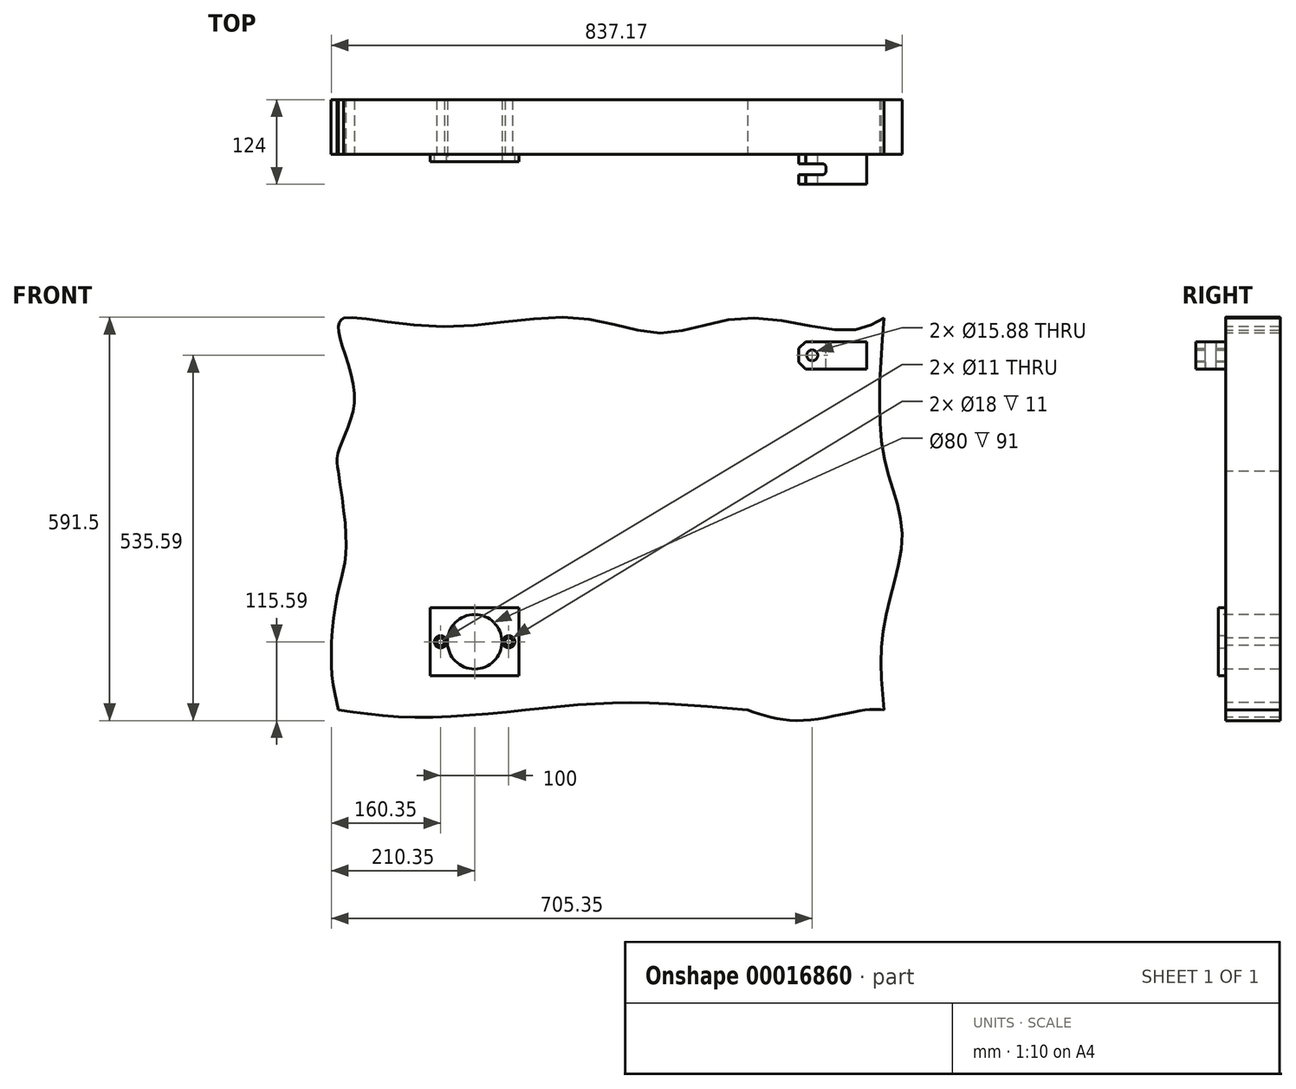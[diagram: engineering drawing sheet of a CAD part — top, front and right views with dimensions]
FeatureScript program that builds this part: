
annotation { "Feature Type Name" : "Feature", "Feature Type Description" : "" }
export const myFeature = defineFeature(function(context is Context, id is Id, definition is map)
    precondition{}
    {
        {
            var Q0;
            Q0=qCreatedBy(makeId("Front.planeOp"),FACE);
            var sketch = newSketch(context, id + "F0", { "sketchPlane" : qUnion([Q0])});
            skPoint(sketch, "E0.rect.middle", {"position": v(0, 0) * mm});
            skFitSpline(sketch, "E1", {"points": [v(-300, 175) * mm, v(-288.67, 56.04) * mm, v(-300, 0) * mm, v(-310.2, -107.97) * mm, v(-300, -175) * mm], "startDerivative": vector(67.45, -453.57) * mm, "endDerivative": vector(63.04, -272.45) * mm});
            skFitSpline(sketch, "E2", {"points": [v(300, -175) * mm, v(120.43, -164.33) * mm, v(-25.86, -175) * mm, v(-186.7, -185.87) * mm, v(-300, -175) * mm], "startDerivative": vector(-676.6, 60.09) * mm, "endDerivative": vector(-491.54, 71) * mm});
            skLineSegment(sketch, "E3", {"start": v(0, 0) * mm, "end": v(0, -225.11) * mm, "construction": true});
            skLineSegment(sketch, "E4", {"start": v(0, 0) * mm, "end": v(412.09, 0) * mm, "construction": true});
            skLineSegment(sketch, "E5.0", {"start": v(0, 400) * mm, "end": v(412.09, 400) * mm, "construction": true});
            skLineSegment(sketch, "E6.0", {"start": v(500, 0) * mm, "end": v(500, -225.11) * mm, "construction": true});
            skFitSpline(sketch, "E7", {"points": [v(-300, 175) * mm, v(-300, 203.47) * mm, v(-276.37, 283.03) * mm, v(-300, 385.32) * mm, v(-292.47, 400) * mm], "startDerivative": vector(-24.62, 139.08) * mm, "endDerivative": vector(79.67, 74.73) * mm});
            skFitSpline(sketch, "E8", {"points": [v(300, -175) * mm, v(377.16, -190.54) * mm, v(471.87, -175) * mm, v(500, -175) * mm], "startDerivative": vector(193.63, -65.98) * mm, "endDerivative": vector(105.88, -11.33) * mm});
            skFitSpline(sketch, "E9", {"points": [v(-292.47, 400) * mm, v(-271.63, 400) * mm, v(-139.98, 387.21) * mm, v(50.4, 400) * mm, v(177.31, 377.74) * mm, v(297.6, 400) * mm, v(448.2, 381.53) * mm, v(500, 400) * mm], "startDerivative": vector(259.87, 21.6) * mm, "endDerivative": vector(420.11, 258.52) * mm});
            skFitSpline(sketch, "E10", {"points": [v(500, 400) * mm, v(500, 197.79) * mm, v(526.8, 82.23) * mm, v(500, -51.31) * mm, v(500, -175) * mm], "startDerivative": vector(-55.22, -736.49) * mm, "endDerivative": vector(47.01, -523.19) * mm});
            skSolve(sketch);
        }
        {
            var Q0;
            Q0=qSketchRegion(id+"F0",true);
            extrude(context, id + "F1", {"entities" : qUnion([Q0]), "oppositeDirection" : true, "depth" : 80 * mm});
        }
        {
            var Q0;
            Q0=makeQuery(id+"F1.opExtrude","CAP_FACE",FACE,{"disambiguationData":[OSD([sQuery(id+"F0.wireOp",EDGE,"E1"),sQuery(id+"F0.wireOp",EDGE,"bc24038a-8613-4d95-baf4-b4a1aed5c15a"),sQuery(id+"F0.wireOp",EDGE,"fdfd1424-a203-45f8-9f44-afd27f2000e9"),sQuery(id+"F0.wireOp",EDGE,"E2")])],"isStart":true});
            var sketch = newSketch(context, id + "F2", { "sketchPlane" : qUnion([Q0])});
            skLineSegment(sketch, "E11", {"start": v(-100, 270) * mm, "end": v(-100, -299.44) * mm, "construction": true});
            skLineSegment(sketch, "E12", {"start": v(-457.85, -75) * mm, "end": v(206.33, -75) * mm, "construction": true});
            skCircle(sketch, "E13", {"center": v(-100, -75) * mm, "radius": 40 * mm});
            skLineSegment(sketch, "E14.0", {"start": v(-150, 270) * mm, "end": v(-150, -299.44) * mm, "construction": true});
            skCircle(sketch, "E15", {"center": v(-150, -75) * mm, "radius": 5.5 * mm});
            skCircle(sketch, "E16.0.MirrorC", {"center": v(-50, -75) * mm, "radius": 5.5 * mm});
            skSolve(sketch);
        }
        {
            var Q0;
            Q0=qSketchRegion(id+"F2",true);
            extrude(context, id + "F3", {"entities" : qUnion([Q0]), "operationType" : NewBodyOperationType.REMOVE, "endBound" : BoundingType.THROUGH_ALL, "oppositeDirection" : true, "depth" : 25 * mm});
        }
        {
            var Q0;
            Q0=makeQuery(id+"F1.opExtrude","CAP_FACE",FACE,{"disambiguationData":[OSD([sQuery(id+"F0.wireOp",EDGE,"E1"),sQuery(id+"F0.wireOp",EDGE,"bc24038a-8613-4d95-baf4-b4a1aed5c15a"),sQuery(id+"F0.wireOp",EDGE,"fdfd1424-a203-45f8-9f44-afd27f2000e9"),sQuery(id+"F0.wireOp",EDGE,"E2")])],"isStart":true});
            var sketch = newSketch(context, id + "F4", { "sketchPlane" : qUnion([Q0])});
            skLineSegment(sketch, "E17", {"start": v(-100, -75) * mm, "end": v(-100, -205.65) * mm, "construction": true});
            skLineSegment(sketch, "E18", {"start": v(-100, -75) * mm, "end": v(-353.74, -75) * mm, "construction": true});
            skLineSegment(sketch, "E19.0", {"start": v(-165, -25) * mm, "end": v(-165, -125) * mm});
            skLineSegment(sketch, "E20.0", {"start": v(-35, -125) * mm, "end": v(-165, -125) * mm});
            skLineSegment(sketch, "E21.0.MirrorCS", {"start": v(-35, -25) * mm, "end": v(-165, -25) * mm});
            skLineSegment(sketch, "E22.0.MirrorCS", {"start": v(-35, -25) * mm, "end": v(-35, -125) * mm});
            skPoint(sketch, "E23.orphan", {"position": v(-165, -75) * mm});
            skPoint(sketch, "E24.orphan", {"position": v(-100, -25) * mm});
            skPoint(sketch, "E25.orphan", {"position": v(-35, -75) * mm});
            skPoint(sketch, "E26.orphan", {"position": v(-100, -125) * mm});
            skPoint(sketch, "E27.orphan", {"position": v(-353.74, -25) * mm});
            skPoint(sketch, "E28.orphan", {"position": v(-353.74, -125) * mm});
            skPoint(sketch, "E29.orphan", {"position": v(-165, -205.65) * mm});
            skPoint(sketch, "E30.orphan", {"position": v(-35, -205.65) * mm});
            skCircle(sketch, "E31.0", {"center": v(-100, -75) * mm, "radius": 40 * mm});
            skCircle(sketch, "E32", {"center": v(-150, -75) * mm, "radius": 9 * mm});
            skCircle(sketch, "E33.0.MirrorC", {"center": v(-50, -75) * mm, "radius": 9 * mm});
            skSolve(sketch);
        }
        {
            var Q0;
            Q0=qSketchRegion(id+"F4",true);
            extrude(context, id + "F5", {"entities" : qUnion([Q0]), "operationType" : NewBodyOperationType.ADD, "depth" : 11 * mm});
        }
        {
            var Q0;
            {var subQ0=sQuery(id+"F0.wireOp",EDGE,"E1");var subQ1=sQuery(id+"F0.wireOp",EDGE,"bc24038a-8613-4d95-baf4-b4a1aed5c15a");var subQ2=sQuery(id+"F0.wireOp",EDGE,"fdfd1424-a203-45f8-9f44-afd27f2000e9");var subQ3=sQuery(id+"F0.wireOp",EDGE,"E2");Q0=makeQuery(id+"F5.boolean.opBoolean","SPLIT",FACE,{"disambiguationData":[TD([makeQuery(id+"F1.opExtrude","SWEPT_FACE",FACE,{"disambiguationData":[OSD([subQ0])]})])],"derivedFrom":makeQuery(id+"F1.opExtrude","CAP_FACE",FACE,{"disambiguationData":[OSD([subQ0,subQ1,subQ2,subQ3])],"isStart":true})});}
            var sketch = newSketch(context, id + "F6", { "sketchPlane" : qUnion([Q0])});
            skCircle(sketch, "E34.0", {"center": v(-100, -75) * mm, "radius": 40 * mm, "construction": true});
            skLineSegment(sketch, "E35", {"start": v(-100, -75) * mm, "end": v(-100, 236.24) * mm, "construction": true});
            skLineSegment(sketch, "E36", {"start": v(-100, -75) * mm, "end": v(374.63, -75) * mm, "construction": true});
            skLineSegment(sketch, "E37.0", {"start": v(375, -75) * mm, "end": v(375, 236.24) * mm, "construction": true});
            skLineSegment(sketch, "E38.0", {"start": v(-100, 325) * mm, "end": v(374.63, 325) * mm, "construction": true});
            skLineSegment(sketch, "E39.0", {"start": v(475, -75) * mm, "end": v(475, 236.24) * mm, "construction": true});
            skLineSegment(sketch, "E40.0", {"start": v(-100, 365) * mm, "end": v(374.63, 365) * mm, "construction": true});
            skLineSegment(sketch, "E41.0", {"start": v(395, 325) * mm, "end": v(395, 365) * mm, "construction": true});
            skLineSegment(sketch, "E42.bottom", {"start": v(375, 365) * mm, "end": v(475, 365) * mm});
            skLineSegment(sketch, "E42.top", {"start": v(375, 325) * mm, "end": v(475, 325) * mm});
            skLineSegment(sketch, "E42.left", {"start": v(375, 365) * mm, "end": v(375, 325) * mm});
            skLineSegment(sketch, "E42.right", {"start": v(475, 365) * mm, "end": v(475, 325) * mm});
            skCircle(sketch, "E43", {"center": v(395, 345) * mm, "radius": 7.94 * mm});
            skSolve(sketch);
        }
        {
            var Q0;
            Q0=qSketchRegion(id+"F6",true);
            extrude(context, id + "F7", {"entities" : qUnion([Q0]), "depth" : 44 * mm});
        }
        {
            var Q0;
            Q0=makeQuery(id+"F7.opExtrude","SWEPT_FACE",FACE,{"disambiguationData":[OSD([sQuery(id+"F6.wireOp",EDGE,"E42.bottom")])]});
            var sketch = newSketch(context, id + "F8", { "sketchPlane" : qUnion([Q0])});
            skLineSegment(sketch, "E44", {"start": v(375, -22) * mm, "end": v(475, -22) * mm, "construction": true});
            skLineSegment(sketch, "E45.0", {"start": v(415, -44) * mm, "end": v(415, 0) * mm, "construction": true});
            skLineSegment(sketch, "E46.0", {"start": v(235, -14) * mm, "end": v(375, -14) * mm, "construction": true});
            skLineSegment(sketch, "E47.bottom", {"start": v(375, -14) * mm, "end": v(415, -14) * mm});
            skLineSegment(sketch, "E47.top", {"start": v(375, -30) * mm, "end": v(415, -30) * mm});
            skLineSegment(sketch, "E47.left", {"start": v(375, -14) * mm, "end": v(375, -30) * mm});
            skLineSegment(sketch, "E47.right", {"start": v(415, -14) * mm, "end": v(415, -30) * mm});
            skSolve(sketch);
        }
        {
            var Q0;
            Q0=qSketchRegion(id+"F8",true);
            extrude(context, id + "F9", {"entities" : qUnion([Q0]), "operationType" : NewBodyOperationType.REMOVE, "endBound" : BoundingType.THROUGH_ALL, "oppositeDirection" : true, "depth" : 25 * mm});
        }
        {
            var Q0;
            {var subQ0=sQuery(id+"F6.wireOp",EDGE,"E42.bottom");var subQ1=sQuery(id+"F6.wireOp",EDGE,"E42.left");Q0=makeQuery(id+"F9.boolean.opBoolean","SPLIT",EDGE,{"disambiguationData":[TD([makeQuery(id+"F9.opExtrude","SWEPT_FACE",FACE,{"disambiguationData":[OSD([sQuery(id+"F8.wireOp",EDGE,"E47.bottom")])]})])],"derivedFrom":makeQuery(id+"F7.opExtrude","SWEPT_EDGE",EDGE,{"disambiguationData":[OSD([subQ0,subQ1])]})});}
            var Q1;
            {var subQ0=sQuery(id+"F6.wireOp",EDGE,"E42.bottom");var subQ1=sQuery(id+"F6.wireOp",EDGE,"E42.left");Q1=makeQuery(id+"F9.boolean.opBoolean","SPLIT",EDGE,{"disambiguationData":[TD([makeQuery(id+"F9.opExtrude","SWEPT_FACE",FACE,{"disambiguationData":[OSD([sQuery(id+"F8.wireOp",EDGE,"E47.top")])]})])],"derivedFrom":makeQuery(id+"F7.opExtrude","SWEPT_EDGE",EDGE,{"disambiguationData":[OSD([subQ0,subQ1])]})});}
            var Q2;
            {var subQ0=sQuery(id+"F6.wireOp",EDGE,"E42.top");var subQ1=sQuery(id+"F6.wireOp",EDGE,"E42.left");Q2=makeQuery(id+"F9.boolean.opBoolean","SPLIT",EDGE,{"disambiguationData":[TD([makeQuery(id+"F9.opExtrude","SWEPT_FACE",FACE,{"disambiguationData":[OSD([sQuery(id+"F8.wireOp",EDGE,"E47.bottom")])]})])],"derivedFrom":makeQuery(id+"F7.opExtrude","SWEPT_EDGE",EDGE,{"disambiguationData":[OSD([subQ0,subQ1])]})});}
            var Q3;
            {var subQ0=sQuery(id+"F6.wireOp",EDGE,"E42.top");var subQ1=sQuery(id+"F6.wireOp",EDGE,"E42.left");Q3=makeQuery(id+"F9.boolean.opBoolean","SPLIT",EDGE,{"disambiguationData":[TD([makeQuery(id+"F9.opExtrude","SWEPT_FACE",FACE,{"disambiguationData":[OSD([sQuery(id+"F8.wireOp",EDGE,"E47.top")])]})])],"derivedFrom":makeQuery(id+"F7.opExtrude","SWEPT_EDGE",EDGE,{"disambiguationData":[OSD([subQ0,subQ1])]})});}
            chamfer(context, id + "F10", {"entities" : qUnion([Q0, Q1, Q2, Q3]), "width" : 10 * mm, "tangentPropagation" : true});
        }
        {
            var Q0;
            Q0=makeQuery(id+"F9.boolean.opBoolean","COPY",EDGE,{"derivedFrom":makeQuery(id+"F9.opExtrude","SWEPT_EDGE",EDGE,{"disambiguationData":[OSD([sQuery(id+"F8.wireOp",EDGE,"E47.bottom"),sQuery(id+"F8.wireOp",EDGE,"E47.right")])]})});
            var Q1;
            Q1=makeQuery(id+"F9.boolean.opBoolean","COPY",EDGE,{"derivedFrom":makeQuery(id+"F9.opExtrude","SWEPT_EDGE",EDGE,{"disambiguationData":[OSD([sQuery(id+"F8.wireOp",EDGE,"E47.top"),sQuery(id+"F8.wireOp",EDGE,"E47.right")])]})});
            fillet(context, id + "F11", {"entities" : qUnion([Q0, Q1]), "radius" : 5 * mm, "tangentPropagation" : true, "allowEdgeOverflow" : false});
        }
    });
